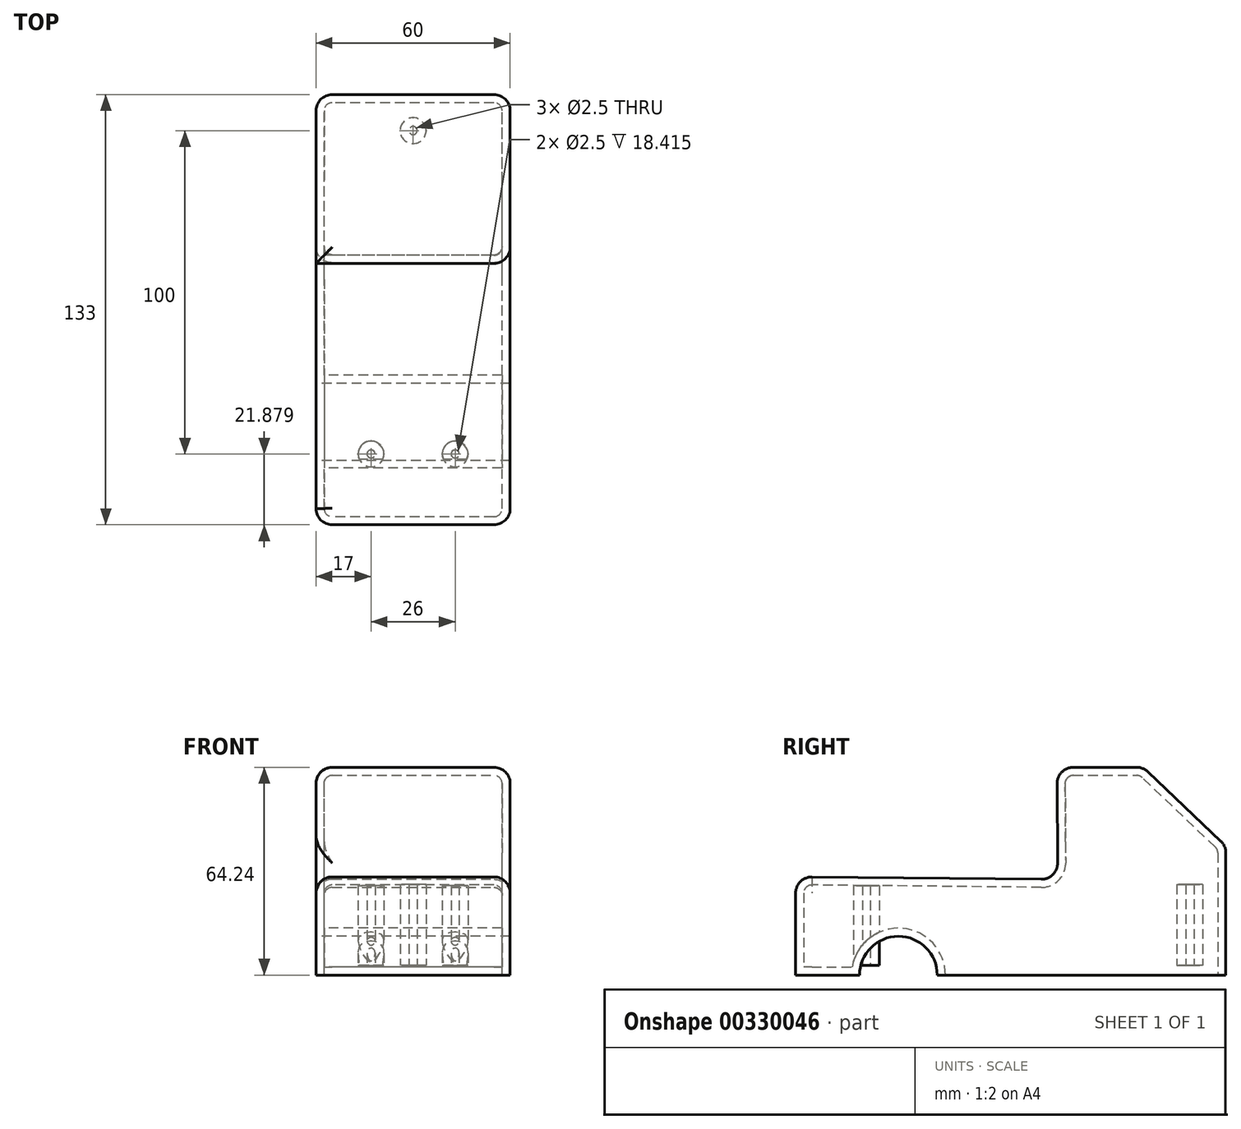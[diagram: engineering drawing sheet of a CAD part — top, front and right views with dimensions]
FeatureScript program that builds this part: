
annotation { "Feature Type Name" : "Feature", "Feature Type Description" : "" }
export const myFeature = defineFeature(function(context is Context, id is Id, definition is map)
    precondition{}
    {
        {
            var Q0;
            Q0=qCreatedBy(makeId("Right.planeOp"),FACE);
            var sketch = newSketch(context, id + "F0", { "sketchPlane" : qUnion([Q0])});
            skLineSegment(sketch, "E0.bottom", {"start": v(-60.6, 0) * mm, "end": v(72.4, 0) * mm});
            skLineSegment(sketch, "E0.top", {"start": v(-60.6, 64.24) * mm, "end": v(72.4, 64.24) * mm});
            skLineSegment(sketch, "E0.left", {"start": v(-60.6, 0) * mm, "end": v(-60.6, 64.24) * mm});
            skLineSegment(sketch, "E0.right", {"start": v(72.4, 0) * mm, "end": v(72.4, 64.24) * mm});
            skCircle(sketch, "E1", {"center": v(-28.83, 0) * mm, "radius": 12 * mm});
            skCircle(sketch, "E2", {"center": v(42.4, 2) * mm, "radius": 12 * mm});
            skLineSegment(sketch, "E3", {"start": v(-60.6, 30.4) * mm, "end": v(20.4, 29.56) * mm});
            skLineSegment(sketch, "E4", {"start": v(20.4, 29.56) * mm, "end": v(20.19, 64.24) * mm});
            skLineSegment(sketch, "E5", {"start": v(46.85, 64.24) * mm, "end": v(72.4, 39.93) * mm});
            skSolve(sketch);
        }
        {
            var Q0;
            Q0=qCreatedBy(makeId("Top.planeOp"),FACE);
            cPlane(context, id + "F1", {"entities" : qUnion([Q0]), "cplaneType" : CPlaneType.OFFSET, "offset" : 3 * mm, "width" : 150 * mm, "height" : 150 * mm});
        }
        {
            var Q0;
            Q0=qCreatedBy(id+"F1.planeOp",FACE);
            var sketch = newSketch(context, id + "F2", { "sketchPlane" : qUnion([Q0])});
            skLineSegment(sketch, "E6", {"start": v(0, 61.27) * mm, "end": v(0, -38.73) * mm, "construction": true});
            skLineSegment(sketch, "E7", {"start": v(0, -38.73) * mm, "end": v(13, -38.73) * mm, "construction": true});
            skCircle(sketch, "E8", {"center": v(0, 61.27) * mm, "radius": 4 * mm});
            skCircle(sketch, "E9", {"center": v(13, -38.73) * mm, "radius": 4 * mm});
            skCircle(sketch, "E10", {"center": v(13, -38.73) * mm, "radius": 1.25 * mm});
            skCircle(sketch, "E11", {"center": v(0, 61.27) * mm, "radius": 1.25 * mm});
            skLineSegment(sketch, "E12.MirrorCS", {"start": v(0, -38.73) * mm, "end": v(-13, -38.73) * mm, "construction": true});
            skCircle(sketch, "E13.MirrorC", {"center": v(-13, -38.73) * mm, "radius": 4 * mm});
            skCircle(sketch, "E14.MirrorC", {"center": v(-13, -38.73) * mm, "radius": 1.25 * mm});
            skSolve(sketch);
        }
        {
            var Q0;
            {var subQ0=sQuery(id+"F0.wireOp",EDGE,"E3");Q0=makeQuery(id+"F0.imprint","IMPRINT",FACE,{"disambiguationData":[TD([[makeQuery(id+"F0.imprint","IMPRINT",EDGE,{"derivedFrom":subQ0}),-1.0]])]});}
            extrude(context, id + "F3", {"entities" : qUnion([Q0]), "endBound" : BoundingType.SYMMETRIC, "depth" : 60 * mm});
        }
        {
            var Q0;
            {var subQ0=sQuery(id+"F0.wireOp",EDGE,"E3");Q0=makeQuery(id+"F0.imprint","IMPRINT",FACE,{"disambiguationData":[TD([[makeQuery(id+"F0.imprint","IMPRINT",EDGE,{"derivedFrom":subQ0}),-1.0]])]});}
            extrude(context, id + "F4", {"entities" : qUnion([Q0]), "operationType" : NewBodyOperationType.ADD, "endBound" : BoundingType.SYMMETRIC, "depth" : 25 * mm});
        }
        {
            var Q0;
            {var subQ0=sQuery(id+"F0.wireOp",EDGE,"E3");Q0=makeQuery(id+"F0.imprint","IMPRINT",FACE,{"disambiguationData":[TD([[makeQuery(id+"F0.imprint","IMPRINT",EDGE,{"derivedFrom":subQ0}),-1.0]])]});}
            extrude(context, id + "F5", {"entities" : qUnion([Q0]), "operationType" : NewBodyOperationType.ADD, "endBound" : BoundingType.SYMMETRIC, "depth" : 25 * mm});
        }
        {
            var Q0;
            {var subQ0=sQuery(id+"F0.wireOp",EDGE,"E3");Q0=makeQuery(id+"F0.imprint","IMPRINT",FACE,{"disambiguationData":[TD([[makeQuery(id+"F0.imprint","IMPRINT",EDGE,{"derivedFrom":subQ0}),-1.0]])]});}
            extrude(context, id + "F6", {"entities" : qUnion([Q0]), "operationType" : NewBodyOperationType.ADD, "endBound" : BoundingType.SYMMETRIC, "depth" : 25 * mm});
        }
        {
            var Q0;
            {var subQ0=sQuery(id+"F0.wireOp",EDGE,"E3");Q0=makeQuery(id+"F0.imprint","IMPRINT",FACE,{"disambiguationData":[TD([[makeQuery(id+"F0.imprint","IMPRINT",EDGE,{"derivedFrom":subQ0}),-1.0]])]});}
            extrude(context, id + "F7", {"entities" : qUnion([Q0]), "operationType" : NewBodyOperationType.ADD, "endBound" : BoundingType.SYMMETRIC, "depth" : 25 * mm});
        }
        {
            var Q0;
            {var subQ0=sQuery(id+"F0.wireOp",EDGE,"E1");var subQ1=sQuery(id+"F0.wireOp",EDGE,"E0.bottom");var subQ2=makeQuery(id+"F0.imprint","INTERSECT",VERTEX,{"disambiguationData":[OD(0.0)],"derivedFrom":[subQ1,subQ0]});Q0=makeQuery(id+"F0.imprint","IMPRINT",FACE,{"disambiguationData":[TD([[makeQuery(id+"F0.imprint","IMPRINT",EDGE,{"disambiguationData":[TD([[subQ2,-1.0]])],"derivedFrom":subQ1}),1.0]])]});}
            var Q1;
            {var subQ0=sQuery(id+"F0.wireOp",EDGE,"E2");var subQ1=sQuery(id+"F0.wireOp",EDGE,"E0.bottom");var subQ2=makeQuery(id+"F0.imprint","INTERSECT",VERTEX,{"disambiguationData":[OD(0.0)],"derivedFrom":[subQ1,subQ0]});Q1=makeQuery(id+"F0.imprint","IMPRINT",FACE,{"disambiguationData":[TD([[makeQuery(id+"F0.imprint","IMPRINT",EDGE,{"disambiguationData":[TD([[subQ2,-1.0]])],"derivedFrom":subQ1}),1.0]])]});}
            extrude(context, id + "F8", {"entities" : qUnion([Q0, Q1]), "operationType" : NewBodyOperationType.ADD, "endBound" : BoundingType.SYMMETRIC, "depth" : 60 * mm});
        }
        {
            var Q0;
            Q0=makeQuery(id+"F3.opExtrude","CAP_EDGE",EDGE,{"disambiguationData":[OSD([sQuery(id+"F0.wireOp",EDGE,"E3")])],"isStart":true});
            var Q1;
            Q1=makeQuery(id+"F3.opExtrude","SWEPT_EDGE",EDGE,{"disambiguationData":[OSD([sQuery(id+"F0.wireOp",EDGE,"E0.left"),sQuery(id+"F0.wireOp",EDGE,"E3")])]});
            var Q2;
            Q2=makeQuery(id+"F3.opExtrude","CAP_EDGE",EDGE,{"disambiguationData":[OSD([sQuery(id+"F0.wireOp",EDGE,"E3")])],"isStart":false});
            var Q3;
            Q3=makeQuery(id+"F3.opExtrude","SWEPT_EDGE",EDGE,{"disambiguationData":[OSD([sQuery(id+"F0.wireOp",EDGE,"E3"),sQuery(id+"F0.wireOp",EDGE,"E4")])]});
            var Q4;
            Q4=makeQuery(id+"F3.opExtrude","SWEPT_EDGE",EDGE,{"disambiguationData":[OSD([sQuery(id+"F0.wireOp",EDGE,"E0.top"),sQuery(id+"F0.wireOp",EDGE,"E4")])]});
            var Q5;
            Q5=makeQuery(id+"F3.opExtrude","CAP_EDGE",EDGE,{"disambiguationData":[OSD([sQuery(id+"F0.wireOp",EDGE,"E0.top")])],"isStart":true});
            var Q6;
            Q6=makeQuery(id+"F3.opExtrude","SWEPT_EDGE",EDGE,{"disambiguationData":[OSD([sQuery(id+"F0.wireOp",EDGE,"E0.top"),sQuery(id+"F0.wireOp",EDGE,"E5")])]});
            var Q7;
            Q7=makeQuery(id+"F3.opExtrude","CAP_EDGE",EDGE,{"disambiguationData":[OSD([sQuery(id+"F0.wireOp",EDGE,"E0.top")])],"isStart":false});
            var Q8;
            Q8=makeQuery(id+"F3.opExtrude","CAP_EDGE",EDGE,{"disambiguationData":[OSD([sQuery(id+"F0.wireOp",EDGE,"E0.left")])],"isStart":true});
            var Q9;
            Q9=makeQuery(id+"F3.opExtrude","CAP_EDGE",EDGE,{"disambiguationData":[OSD([sQuery(id+"F0.wireOp",EDGE,"E0.left")])],"isStart":false});
            var Q10;
            Q10=makeQuery(id+"F3.opExtrude","CAP_EDGE",EDGE,{"disambiguationData":[OSD([sQuery(id+"F0.wireOp",EDGE,"E5")])],"isStart":true});
            var Q11;
            Q11=makeQuery(id+"F3.opExtrude","CAP_EDGE",EDGE,{"disambiguationData":[OSD([sQuery(id+"F0.wireOp",EDGE,"E0.right")])],"isStart":true});
            var Q12;
            Q12=makeQuery(id+"F3.opExtrude","SWEPT_EDGE",EDGE,{"disambiguationData":[OSD([sQuery(id+"F0.wireOp",EDGE,"E0.right"),sQuery(id+"F0.wireOp",EDGE,"E5")])]});
            var Q13;
            Q13=makeQuery(id+"F3.opExtrude","CAP_EDGE",EDGE,{"disambiguationData":[OSD([sQuery(id+"F0.wireOp",EDGE,"E5")])],"isStart":false});
            var Q14;
            Q14=makeQuery(id+"F3.opExtrude","CAP_EDGE",EDGE,{"disambiguationData":[OSD([sQuery(id+"F0.wireOp",EDGE,"E0.right")])],"isStart":false});
            var Q15;
            Q15=makeQuery(id+"F3.opExtrude","CAP_EDGE",EDGE,{"disambiguationData":[OSD([sQuery(id+"F0.wireOp",EDGE,"E4")])],"isStart":false});
            fillet(context, id + "F9", {"entities" : qUnion([Q0, Q1, Q2, Q3, Q4, Q5, Q6, Q7, Q8, Q9, Q10, Q11, Q12, Q13, Q14, Q15]), "radius" : 5 * mm, "tangentPropagation" : true, "allowEdgeOverflow" : false});
        }
        {
            var Q0;
            {var subQ0=sQuery(id+"F0.wireOp",EDGE,"E2");var subQ1=sQuery(id+"F0.wireOp",EDGE,"E0.bottom");var subQ2=makeQuery(id+"F0.imprint","INTERSECT",VERTEX,{"disambiguationData":[OD(0.0)],"derivedFrom":[subQ1,subQ0]});var subQ4=sQuery(id+"F0.wireOp",EDGE,"E1");var subQ5=makeQuery(id+"F0.imprint","INTERSECT",VERTEX,{"disambiguationData":[OD(0.0)],"derivedFrom":[subQ1,subQ4]});var subQ6=makeQuery(id+"F0.imprint","INTERSECT",VERTEX,{"disambiguationData":[OD(1.0)],"derivedFrom":[subQ1,subQ4]});Q0=makeQuery(id+"F8.boolean.opBoolean","MERGE",FACE,{"derivedFrom":[makeQuery(id+"F3.opExtrude","SWEPT_FACE",FACE,{"disambiguationData":[OSD([subQ1]),TDD([makeQuery(id+"F0.imprint","IMPRINT",EDGE,{"disambiguationData":[TD([[makeQuery(id+"F0.imprint","INTERSECT",VERTEX,{"derivedFrom":[subQ1,sQuery(id+"F0.wireOp",EDGE,"E0.left")]}),-1.0]])],"derivedFrom":subQ1})])]}),makeQuery(id+"F3.opExtrude","SWEPT_FACE",FACE,{"disambiguationData":[OSD([subQ1]),TDD([makeQuery(id+"F0.imprint","IMPRINT",EDGE,{"disambiguationData":[TD([[subQ6,-1.0]])],"derivedFrom":subQ1})])]}),makeQuery(id+"F3.opExtrude","SWEPT_FACE",FACE,{"disambiguationData":[OSD([subQ1]),TDD([makeQuery(id+"F0.imprint","IMPRINT",EDGE,{"disambiguationData":[TD([[makeQuery(id+"F0.imprint","INTERSECT",VERTEX,{"derivedFrom":[subQ1,sQuery(id+"F0.wireOp",EDGE,"E0.right")]}),1.0]])],"derivedFrom":subQ1})])]}),makeQuery(id+"F8.opExtrude","SWEPT_FACE",FACE,{"disambiguationData":[OSD([subQ1]),TDD([makeQuery(id+"F0.imprint","IMPRINT",EDGE,{"disambiguationData":[TD([[subQ5,-1.0]])],"derivedFrom":subQ1})])]}),makeQuery(id+"F8.opExtrude","SWEPT_FACE",FACE,{"disambiguationData":[OSD([subQ1]),TDD([makeQuery(id+"F0.imprint","IMPRINT",EDGE,{"disambiguationData":[TD([[subQ2,-1.0]])],"derivedFrom":subQ1})])]})]});}
            shell(context, id + "F10", {"entities" : qUnion([Q0]), "thickness" : 2.5 * mm});
        }
        {
            var Q0;
            Q0 = qSketchRegion(id + "F2", true);
            extrude(context, id + "F11", {"entities" : qUnion([Q0]), "operationType" : NewBodyOperationType.ADD, "depth" : 25 * mm});
        }
    });
